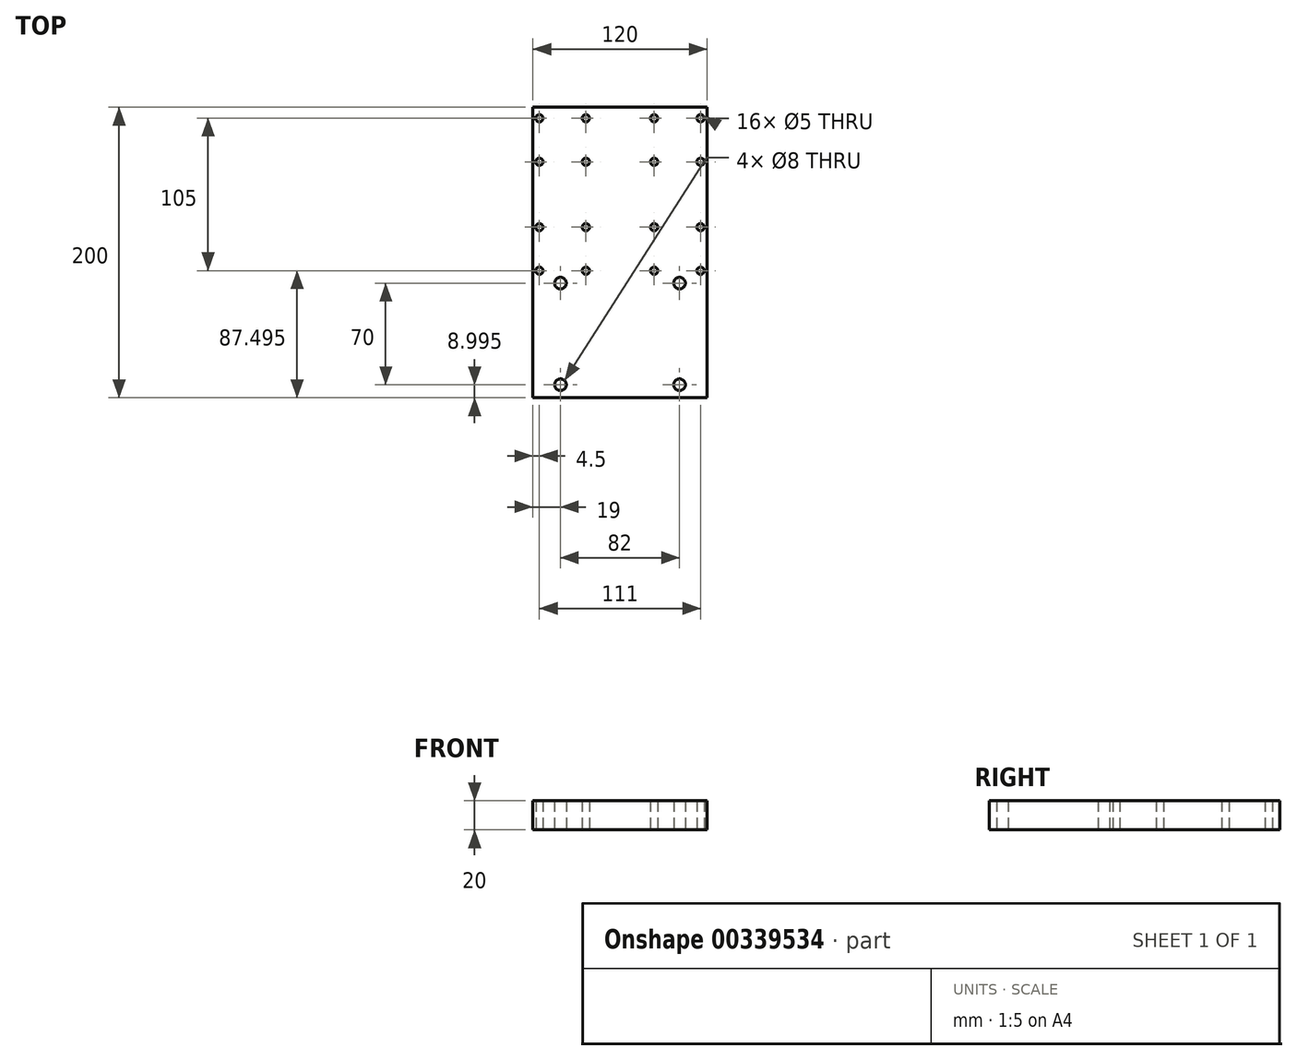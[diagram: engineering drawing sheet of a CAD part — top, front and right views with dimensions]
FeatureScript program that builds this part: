
annotation { "Feature Type Name" : "Feature", "Feature Type Description" : "" }
export const myFeature = defineFeature(function(context is Context, id is Id, definition is map)
    precondition{}
    {
        {
            var Q0;
            Q0=qCreatedBy(makeId("Top.planeOp"),FACE);
            var sketch = newSketch(context, id + "F0", { "sketchPlane" : qUnion([Q0])});
            skLineSegment(sketch, "E0.bottom", {"start": v(-60, 155.37) * mm, "end": v(60, 155.37) * mm});
            skLineSegment(sketch, "E0.top", {"start": v(-60, -44.63) * mm, "end": v(60, -44.63) * mm});
            skLineSegment(sketch, "E0.left", {"start": v(-60, 155.37) * mm, "end": v(-60, -44.63) * mm});
            skLineSegment(sketch, "E0.right", {"start": v(60, 155.37) * mm, "end": v(60, -44.63) * mm});
            skLineSegment(sketch, "E1", {"start": v(-60, 35.37) * mm, "end": v(60, 35.37) * mm, "construction": true});
            skLineSegment(sketch, "E2", {"start": v(0, -44.63) * mm, "end": v(0, 155.37) * mm, "construction": true});
            skPoint(sketch, "E2.startSnap0", {"position": v(0, -44.63) * mm});
            skLineSegment(sketch, "E3", {"start": v(-60, 147.87) * mm, "end": v(60, 147.87) * mm, "construction": true});
            skLineSegment(sketch, "E4", {"start": v(-23.5, 155.37) * mm, "end": v(-23.5, 35.37) * mm, "construction": true});
            skLineSegment(sketch, "E5", {"start": v(-55.5, 155.37) * mm, "end": v(-55.5, 35.37) * mm, "construction": true});
            skLineSegment(sketch, "E6", {"start": v(55.5, 155.37) * mm, "end": v(55.5, 35.37) * mm, "construction": true});
            skLineSegment(sketch, "E7", {"start": v(23.5, 155.37) * mm, "end": v(23.5, 35.37) * mm, "construction": true});
            skLineSegment(sketch, "E8", {"start": v(-60, 117.87) * mm, "end": v(60, 117.87) * mm, "construction": true});
            skLineSegment(sketch, "E9", {"start": v(-60, 72.87) * mm, "end": v(60, 72.87) * mm, "construction": true});
            skLineSegment(sketch, "E10", {"start": v(-60, 42.87) * mm, "end": v(60, 42.87) * mm, "construction": true});
            skLineSegment(sketch, "E11", {"start": v(-39.5, 155.37) * mm, "end": v(-39.5, 35.37) * mm, "construction": true});
            skLineSegment(sketch, "E12", {"start": v(39.5, 155.37) * mm, "end": v(39.5, 35.37) * mm, "construction": true});
            skLineSegment(sketch, "E13", {"start": v(-60, -35.63) * mm, "end": v(60, -35.63) * mm, "construction": true});
            skLineSegment(sketch, "E14", {"start": v(-60, 34.37) * mm, "end": v(60, 34.37) * mm, "construction": true});
            skCircle(sketch, "E15", {"center": v(-41, -35.63) * mm, "radius": 4 * mm});
            skCircle(sketch, "E16", {"center": v(41, -35.63) * mm, "radius": 4 * mm});
            skCircle(sketch, "E17", {"center": v(-41, 34.37) * mm, "radius": 4 * mm});
            skCircle(sketch, "E18", {"center": v(41, 34.37) * mm, "radius": 4 * mm});
            skCircle(sketch, "E19", {"center": v(-55.5, 147.87) * mm, "radius": 2.5 * mm});
            skCircle(sketch, "E20", {"center": v(-23.5, 147.87) * mm, "radius": 2.5 * mm});
            skCircle(sketch, "E21", {"center": v(-55.5, 117.87) * mm, "radius": 2.5 * mm});
            skCircle(sketch, "E22", {"center": v(-23.5, 117.87) * mm, "radius": 2.5 * mm});
            skCircle(sketch, "E23", {"center": v(23.5, 147.87) * mm, "radius": 2.5 * mm});
            skCircle(sketch, "E24", {"center": v(23.5, 117.87) * mm, "radius": 2.5 * mm});
            skCircle(sketch, "E25", {"center": v(55.5, 147.87) * mm, "radius": 2.5 * mm});
            skCircle(sketch, "E26", {"center": v(55.5, 117.87) * mm, "radius": 2.5 * mm});
            skCircle(sketch, "E27", {"center": v(-55.5, 72.87) * mm, "radius": 2.5 * mm});
            skCircle(sketch, "E28", {"center": v(-23.5, 72.87) * mm, "radius": 2.5 * mm});
            skCircle(sketch, "E29", {"center": v(-55.5, 42.87) * mm, "radius": 2.5 * mm});
            skCircle(sketch, "E30", {"center": v(-23.5, 42.87) * mm, "radius": 2.5 * mm});
            skCircle(sketch, "E31", {"center": v(23.5, 42.87) * mm, "radius": 2.5 * mm});
            skCircle(sketch, "E32", {"center": v(23.5, 72.87) * mm, "radius": 2.5 * mm});
            skCircle(sketch, "E33", {"center": v(55.5, 72.87) * mm, "radius": 2.5 * mm});
            skCircle(sketch, "E34", {"center": v(55.5, 42.87) * mm, "radius": 2.5 * mm});
            skSolve(sketch);
        }
        {
            var Q0;
            Q0 = qSketchRegion(id + "F0", true);
            extrude(context, id + "F1", {"entities" : qUnion([Q0]), "depth" : 20 * mm});
        }
    });
